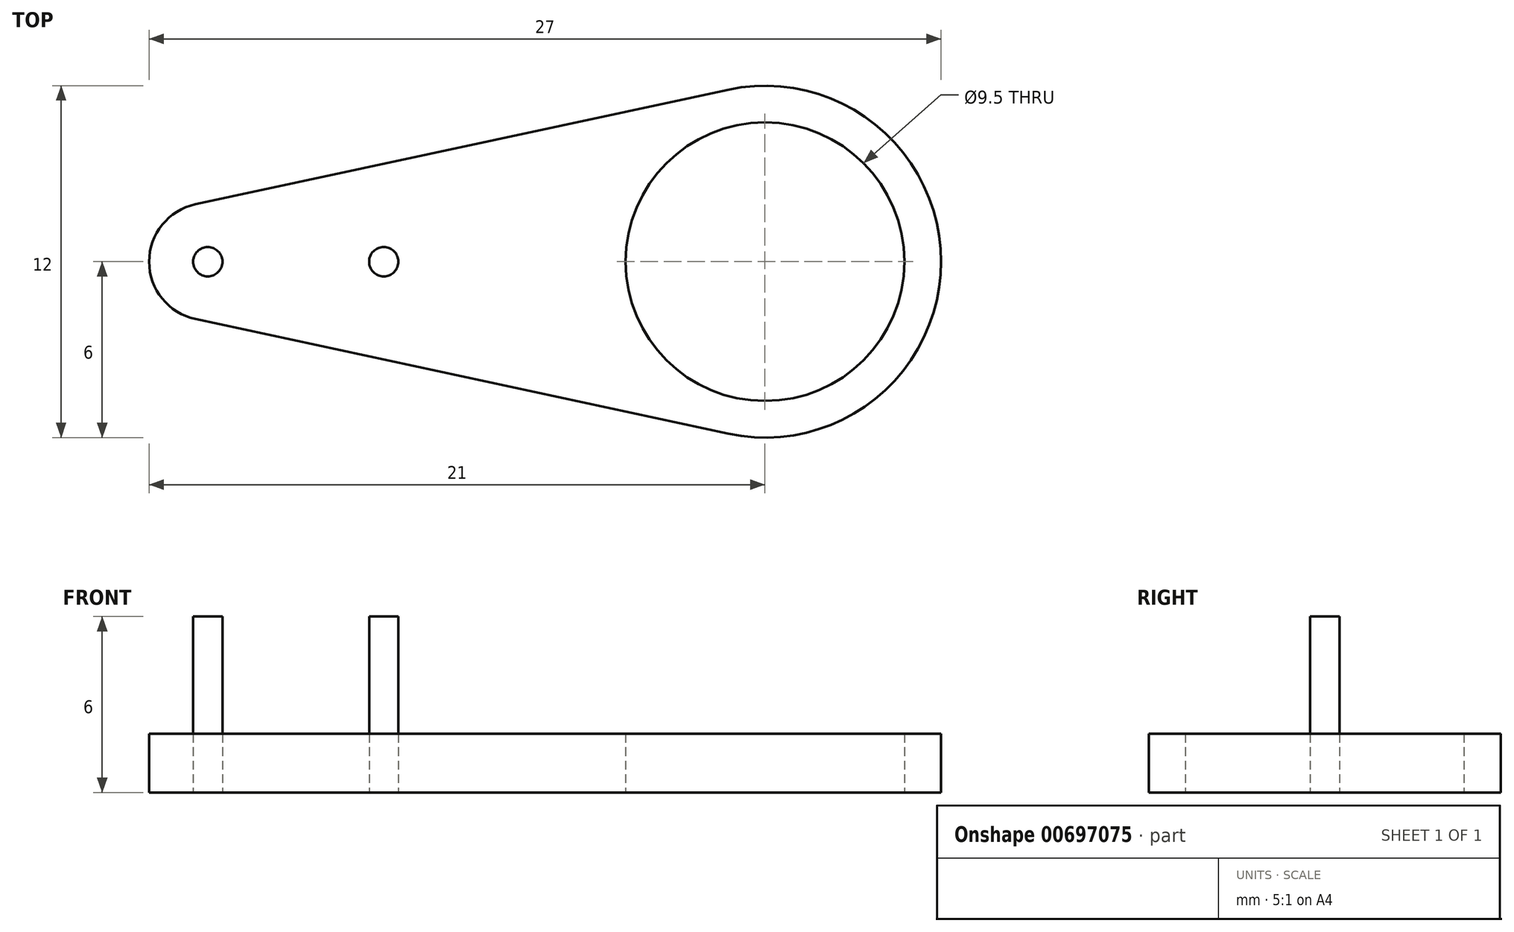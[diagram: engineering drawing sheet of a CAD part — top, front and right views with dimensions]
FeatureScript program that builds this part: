
annotation { "Feature Type Name" : "Feature", "Feature Type Description" : "" }
export const myFeature = defineFeature(function(context is Context, id is Id, definition is map)
    precondition{}
    {
        {
            var Q0;
            Q0=qCreatedBy(makeId("Top.planeOp"),FACE);
            var sketch = newSketch(context, id + "F0", { "sketchPlane" : qUnion([Q0])});
            skCircle(sketch, "E0", {"center": v(3, 0) * mm, "radius": 0.5 * mm});
            skCircle(sketch, "E1", {"center": v(-3, 0) * mm, "radius": 0.5 * mm});
            skSolve(sketch);
        }
        {
            var Q0;
            Q0 = qSketchRegion(id + "F0", true);
            extrude(context, id + "F1", {"entities" : qUnion([Q0]), "depth" : 6 * mm, "offsetDistance" : 25 * mm});
        }
        {
            var Q0;
            Q0=qCreatedBy(makeId("Top.planeOp"),FACE);
            var sketch = newSketch(context, id + "F2", { "sketchPlane" : qUnion([Q0])});
            skCircle(sketch, "E2", {"center": v(16, 0) * mm, "radius": 4.75 * mm});
            skArc(sketch, "E3", {"start": v(14.74, -5.87) * mm, "mid": v(22, 0) * mm, "end": v(14.74, 5.87) * mm});
            skArc(sketch, "E4", {"start": v(-3.42, 1.96) * mm, "mid": v(-5, 0) * mm, "end": v(-3.42, -1.96) * mm});
            skLineSegment(sketch, "E5", {"start": v(-3.42, 1.96) * mm, "end": v(14.74, 5.87) * mm});
            skLineSegment(sketch, "E6", {"start": v(-3.42, -1.96) * mm, "end": v(14.74, -5.87) * mm});
            skSolve(sketch);
        }
        {
            var Q0;
            Q0 = qSketchRegion(id + "F2", true);
            extrude(context, id + "F3", {"entities" : qUnion([Q0]), "depth" : 2 * mm, "offsetDistance" : 25 * mm});
        }
    });
